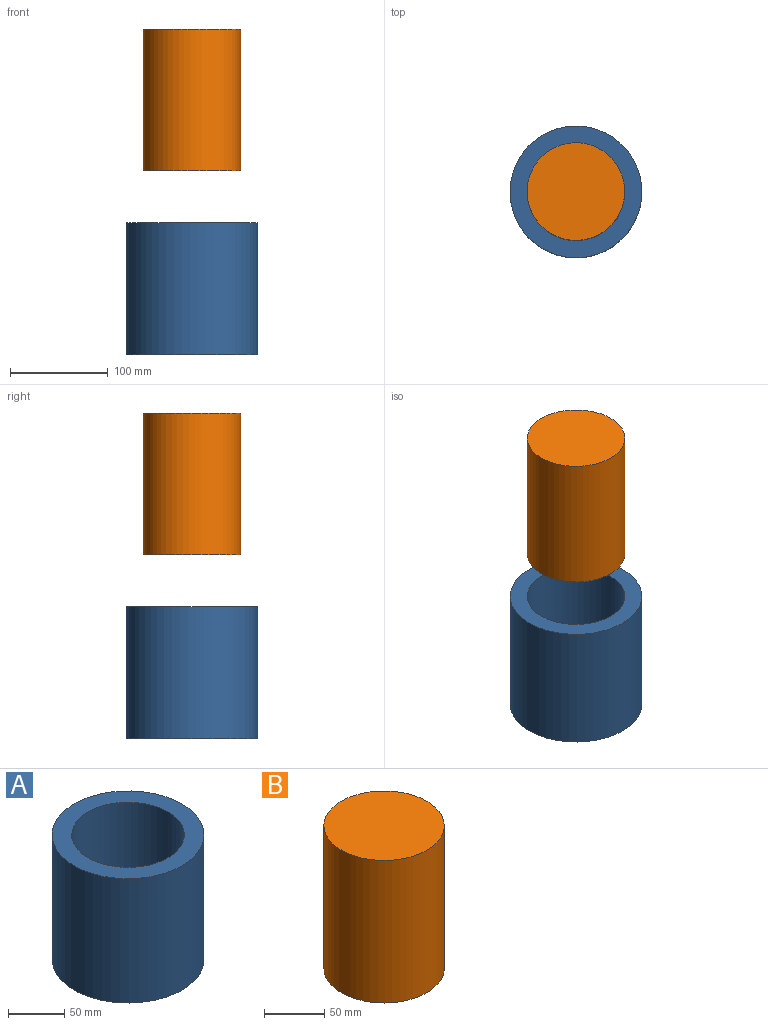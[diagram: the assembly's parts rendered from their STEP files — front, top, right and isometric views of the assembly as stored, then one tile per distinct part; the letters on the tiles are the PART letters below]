
ASSEMBLY  parts=2 mates=1
PART A: 5 faces, bbox 134.9x134.9x135 mm
  f0: cylinder r=67.43mm len=135mm, axis (0,0,-1), area 57194.3mm2, adj f1,f2
  f1: plane 134.86x134.86mm, normal (0,0,1), area 6429.3mm2, adj f0,f3
  f2: plane 134.86x134.86mm, normal (0,0,-1), area 14283.3mm2, adj f0
  f3: cylinder r=50mm len=130mm, axis (0,0,1), area 40840.7mm2, adj f1,f4
  f4: plane 100x100mm, normal (0,0,1), area 7854mm2, adj f3
PART B: 3 faces, bbox 100x100x145 mm
  f0: cylinder r=50mm len=145mm, axis (0,0,-1), area 45553.1mm2, adj f1,f2
  f1: plane 100x100mm, normal (0,0,1), area 7854mm2, adj f0
  f2: plane 100x100mm, normal (0,0,-1), area 7854mm2, adj f0
PLACE A t=(41.91,81.76,-121.16)mm fixed
PLACE B t=(41.91,81.76,67.09)mm
MATE slider A.f3 <-> B.f0  axis (0,0,1) through (41.91,81.76,13.84)mm
